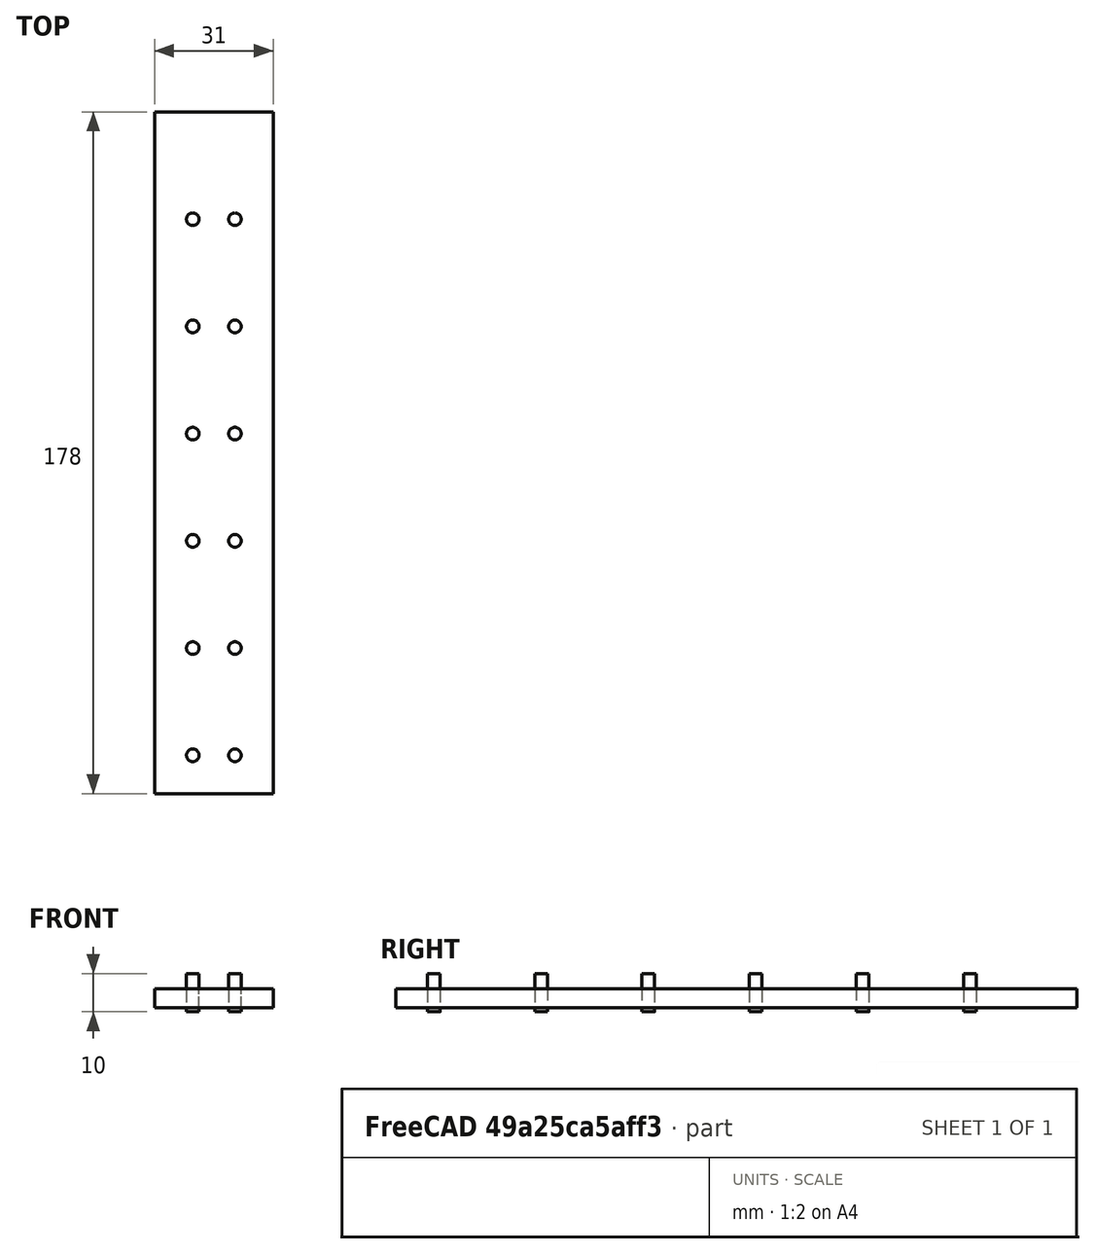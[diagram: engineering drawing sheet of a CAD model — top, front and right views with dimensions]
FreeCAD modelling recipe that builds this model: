
FCSTD DOCUMENT  (FreeCAD 0.20R29177 +426 (Git))
Label: base_valves
License: All rights reserved
LicenseURL: http://en.wikipedia.org/wiki/All_rights_reserved
objects: Part::Cylinder×12, Part::Box×1
note: 13 computed .brp shape members not serialized (recipe doc carries the construction recipe); baked Part::Feature solids carry a one-line shape summary decoded from their .brp

FEATURE [Part::Box] base
  AttacherType = Attacher::AttachEngine3D
  Height = 5
  Length = 31
  Placement = pos=(-10,-10,0) rot=(0,0,1;0rad)
  Width = 178
FEATURE [Part::Cylinder] screw0
  Angle = 360
  AttacherType = Attacher::AttachEngine3D
  FirstAngle = 0
  Height = 10
  Placement = pos=(0,0,-1) rot=(0,0,1;0rad)
  Radius = 1.65
  SecondAngle = 0
FEATURE [Part::Cylinder] screw0001
  Angle = 360
  AttacherType = Attacher::AttachEngine3D
  FirstAngle = 0
  Height = 10
  Placement = pos=(11,0,-1) rot=(0,0,1;0rad)
  Radius = 1.65
  SecondAngle = 0
FEATURE [Part::Cylinder] screw1
  Angle = 360
  AttacherType = Attacher::AttachEngine3D
  FirstAngle = 0
  Height = 10
  Placement = pos=(0,28,-1) rot=(0,0,1;0rad)
  Radius = 1.65
  SecondAngle = 0
FEATURE [Part::Cylinder] screw1001
  Angle = 360
  AttacherType = Attacher::AttachEngine3D
  FirstAngle = 0
  Height = 10
  Placement = pos=(11,28,-1) rot=(0,0,1;0rad)
  Radius = 1.65
  SecondAngle = 0
FEATURE [Part::Cylinder] screw2
  Angle = 360
  AttacherType = Attacher::AttachEngine3D
  FirstAngle = 0
  Height = 10
  Placement = pos=(0,56,-1) rot=(0,0,1;0rad)
  Radius = 1.65
  SecondAngle = 0
FEATURE [Part::Cylinder] screw2001
  Angle = 360
  AttacherType = Attacher::AttachEngine3D
  FirstAngle = 0
  Height = 10
  Placement = pos=(11,56,-1) rot=(0,0,1;0rad)
  Radius = 1.65
  SecondAngle = 0
FEATURE [Part::Cylinder] screw3
  Angle = 360
  AttacherType = Attacher::AttachEngine3D
  FirstAngle = 0
  Height = 10
  Placement = pos=(0,84,-1) rot=(0,0,1;0rad)
  Radius = 1.65
  SecondAngle = 0
FEATURE [Part::Cylinder] screw3001
  Angle = 360
  AttacherType = Attacher::AttachEngine3D
  FirstAngle = 0
  Height = 10
  Placement = pos=(11,84,-1) rot=(0,0,1;0rad)
  Radius = 1.65
  SecondAngle = 0
FEATURE [Part::Cylinder] screw4
  Angle = 360
  AttacherType = Attacher::AttachEngine3D
  FirstAngle = 0
  Height = 10
  Placement = pos=(0,112,-1) rot=(0,0,1;0rad)
  Radius = 1.65
  SecondAngle = 0
FEATURE [Part::Cylinder] screw4001
  Angle = 360
  AttacherType = Attacher::AttachEngine3D
  FirstAngle = 0
  Height = 10
  Placement = pos=(11,112,-1) rot=(0,0,1;0rad)
  Radius = 1.65
  SecondAngle = 0
FEATURE [Part::Cylinder] screw5
  Angle = 360
  AttacherType = Attacher::AttachEngine3D
  FirstAngle = 0
  Height = 10
  Placement = pos=(0,140,-1) rot=(0,0,1;0rad)
  Radius = 1.65
  SecondAngle = 0
FEATURE [Part::Cylinder] screw5001
  Angle = 360
  AttacherType = Attacher::AttachEngine3D
  FirstAngle = 0
  Height = 10
  Placement = pos=(11,140,-1) rot=(0,0,1;0rad)
  Radius = 1.65
  SecondAngle = 0
